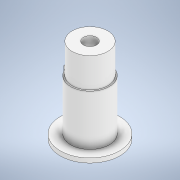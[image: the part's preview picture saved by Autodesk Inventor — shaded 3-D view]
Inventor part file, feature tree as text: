
AUTODESK INVENTOR PART (.ipt)
format: ipt  version: 2020 (Build 240168000, 168)  size: 148,992 bytes
history: native  units: mm
features: sketch x5, extrude x4, hole x1
ambient origin geometry x8: Origin, YZ Plane, XZ Plane, XY Plane, X Axis, Y Axis, Z Axis, Center Point
bodies: Solid1 (feature_tree)
feature tree (10):
  extrude  "Extrusion1"  Depth=17.0mm TaperAngle=0.0deg
  extrude  "Extrusion2"  Depth=1.5mm TaperAngle=0.0deg
  extrude  "Extrusion3"  Depth=3.0mm
  hole  "Hole1"  [1 undecoded]
  extrude  "Extrusion4"  Depth=10.0mm
  sketch  "Sketch1"  dims[d0=13.0mm d1=17.0mm d2=0.0mm]
  sketch  "Sketch2"  dims[d3=20.0mm d4=1.5mm d5=0.0mm]
  sketch  "Sketch4"  dims[d8=1.0mm d9=3.0mm]
  sketch  "Sketch5"  dims[d10=12.0mm d11=10.0mm d12=0.0mm]
  sketch  "Sketch6"  dims[d13=4.5mm d14=6.0mm d15=11.0mm d16=2.6mm d17=90.0deg d18=10.0mm d19=20.594885mm d21=1.5mm d24=10.0mm d25=0.0mm d26=4.0mm]
note: 1 required parameter value undecoded (feature->parameter linkage not recoverable at this tier; creation-order binding heuristic only, values carry confidence <= 0.55)
